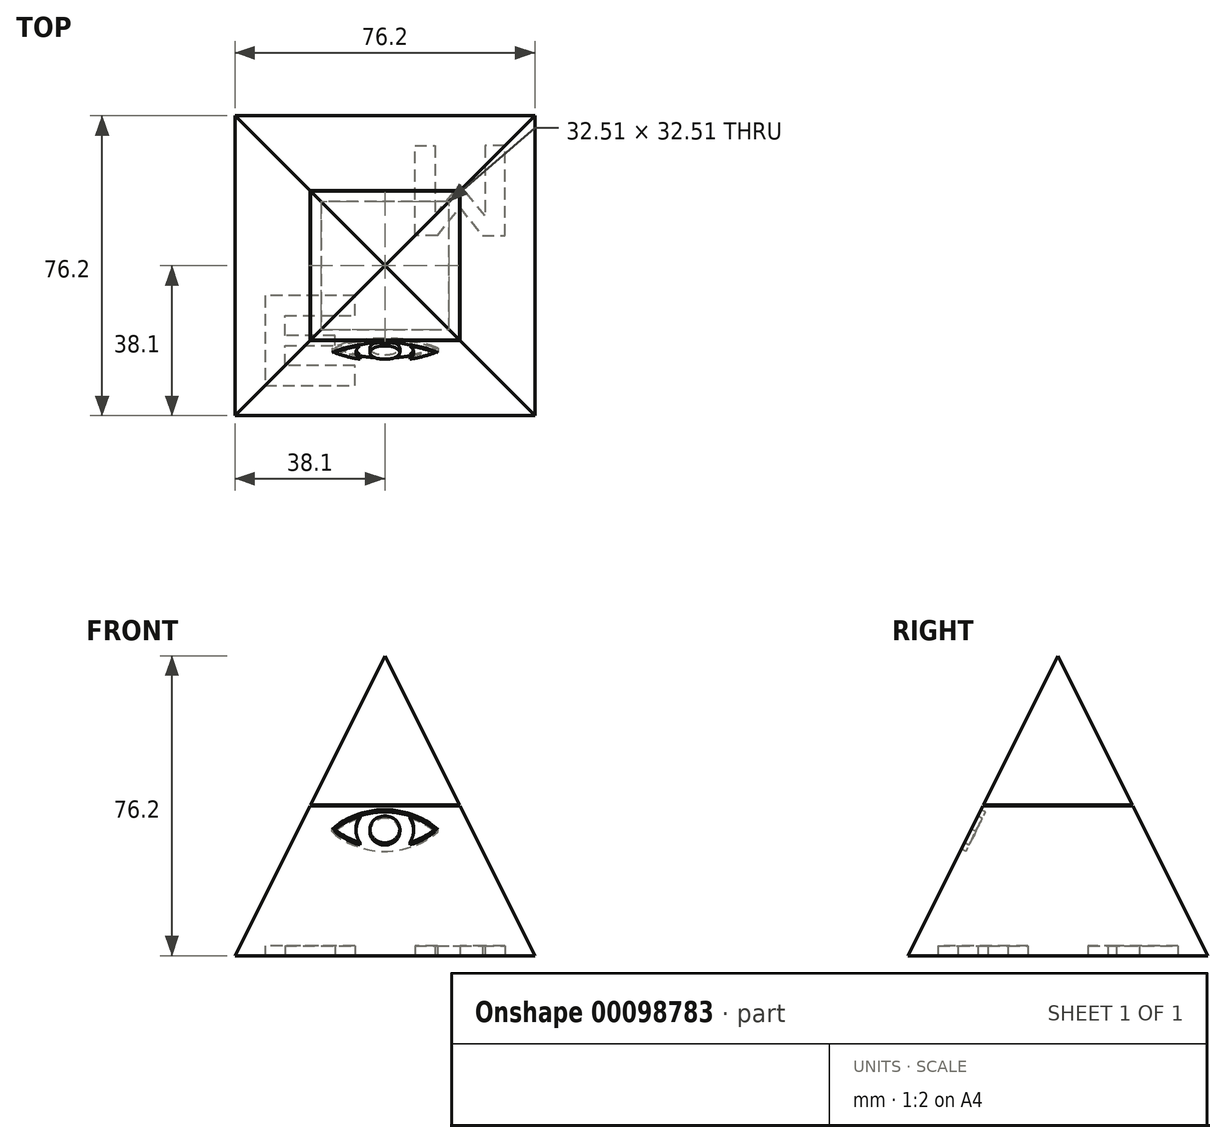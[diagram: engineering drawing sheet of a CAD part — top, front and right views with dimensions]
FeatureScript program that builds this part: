
annotation { "Feature Type Name" : "Feature", "Feature Type Description" : "" }
export const myFeature = defineFeature(function(context is Context, id is Id, definition is map)
    precondition{}
    {
        {
            var Q0;
            Q0=qCreatedBy(makeId("Front.planeOp"),FACE);
            var sketch = newSketch(context, id + "F0", { "sketchPlane" : qUnion([Q0])});
            skLineSegment(sketch, "E0", {"start": v(-38.1, 0) * mm, "end": v(-38.1, 38.1) * mm});
            skLineSegment(sketch, "E1", {"start": v(-38.1, 38.1) * mm, "end": v(0, 38.1) * mm});
            skLineSegment(sketch, "E2", {"start": v(0, 38.1) * mm, "end": v(38.1, 38.1) * mm});
            skLineSegment(sketch, "E3", {"start": v(38.1, 38.1) * mm, "end": v(38.1, 0) * mm});
            skLineSegment(sketch, "E4", {"start": v(38.1, 0) * mm, "end": v(38.1, -38.1) * mm});
            skLineSegment(sketch, "E5", {"start": v(38.1, -38.1) * mm, "end": v(0, -38.1) * mm});
            skLineSegment(sketch, "E6", {"start": v(0, -38.1) * mm, "end": v(-38.1, -38.1) * mm});
            skLineSegment(sketch, "E7", {"start": v(-38.1, -38.1) * mm, "end": v(-38.1, 0) * mm});
            skSolve(sketch);
        }
        {
            var Q0;
            Q0 = qSketchRegion(id + "F0", true);
            extrude(context, id + "F1", {"entities" : qUnion([Q0]), "depth" : 38.1 * mm});
        }
        {
            var Q0;
            Q0 = qSketchRegion(id + "F0", true);
            extrude(context, id + "F2", {"entities" : qUnion([Q0]), "operationType" : NewBodyOperationType.ADD, "oppositeDirection" : true, "depth" : 38.1 * mm});
        }
        {
            var Q0;
            Q0=makeQuery(id+"F1.opExtrude","CAP_FACE",FACE,{"disambiguationData":[OSD([sQuery(id+"F0.wireOp",EDGE,"E0"),sQuery(id+"F0.wireOp",EDGE,"E1"),sQuery(id+"F0.wireOp",EDGE,"E2"),sQuery(id+"F0.wireOp",EDGE,"E3"),sQuery(id+"F0.wireOp",EDGE,"E4"),sQuery(id+"F0.wireOp",EDGE,"E5"),sQuery(id+"F0.wireOp",EDGE,"E6"),sQuery(id+"F0.wireOp",EDGE,"E7")])],"isStart":false});
            var sketch = newSketch(context, id + "F3", { "sketchPlane" : qUnion([Q0])});
            skLineSegment(sketch, "E8", {"start": v(-38.1, -38.1) * mm, "end": v(0, 38.1) * mm});
            skLineSegment(sketch, "E9", {"start": v(0, 38.1) * mm, "end": v(38.1, -38.1) * mm});
            skLineSegment(sketch, "E10", {"start": v(38.1, -38.1) * mm, "end": v(-38.1, -38.1) * mm});
            skSolve(sketch);
        }
        {
            var Q0;
            {var subQ0=sQuery(id+"F0.wireOp",EDGE,"E7");var subQ1=sQuery(id+"F0.wireOp",EDGE,"E0");Q0=makeQuery(id+"F2.boolean.opBoolean","MERGE",FACE,{"derivedFrom":[makeQuery(id+"F1.opExtrude","SWEPT_FACE",FACE,{"disambiguationData":[OSD([subQ1,subQ0])]}),makeQuery(id+"F2.opExtrude","SWEPT_FACE",FACE,{"disambiguationData":[OSD([subQ1,subQ0])]})]});}
            var sketch = newSketch(context, id + "F4", { "sketchPlane" : qUnion([Q0])});
            skLineSegment(sketch, "E11", {"start": v(-38.1, -38.1) * mm, "end": v(0, 38.1) * mm});
            skLineSegment(sketch, "E12", {"start": v(0, 38.1) * mm, "end": v(38.1, -38.1) * mm});
            skLineSegment(sketch, "E13", {"start": v(38.1, -38.1) * mm, "end": v(-38.1, -38.1) * mm});
            skSolve(sketch);
        }
        {
            var Q0;
            {var subQ0=sQuery(id+"F4.wireOp",EDGE,"E11");Q0=makeQuery(id+"F4.imprint","IMPRINT",FACE,{"disambiguationData":[TD([[makeQuery(id+"F4.imprint","IMPRINT",EDGE,{"derivedFrom":subQ0}),1.0]])]});}
            var Q1;
            {var subQ0=sQuery(id+"F4.wireOp",EDGE,"E12");Q1=makeQuery(id+"F4.imprint","IMPRINT",FACE,{"disambiguationData":[TD([[makeQuery(id+"F4.imprint","IMPRINT",EDGE,{"derivedFrom":subQ0}),1.0]])]});}
            extrude(context, id + "F5", {"entities" : qUnion([Q0, Q1]), "operationType" : NewBodyOperationType.REMOVE, "oppositeDirection" : true, "depth" : 76.2 * mm});
        }
        {
            var Q0;
            {var subQ0=sQuery(id+"F3.wireOp",EDGE,"E8");Q0=makeQuery(id+"F3.imprint","IMPRINT",FACE,{"disambiguationData":[TD([[makeQuery(id+"F3.imprint","IMPRINT",EDGE,{"derivedFrom":subQ0}),1.0]])]});}
            var Q1;
            {var subQ0=sQuery(id+"F3.wireOp",EDGE,"E9");Q1=makeQuery(id+"F3.imprint","IMPRINT",FACE,{"disambiguationData":[TD([[makeQuery(id+"F3.imprint","IMPRINT",EDGE,{"derivedFrom":subQ0}),1.0]])]});}
            extrude(context, id + "F6", {"entities" : qUnion([Q0, Q1]), "operationType" : NewBodyOperationType.REMOVE, "oppositeDirection" : true, "depth" : 76.2 * mm});
        }
        {
            var Q0;
            Q0=makeQuery(id+"F5.boolean.opBoolean","COPY",FACE,{"derivedFrom":makeQuery(id+"F5.opExtrude","SWEPT_FACE",FACE,{"disambiguationData":[OSD([sQuery(id+"F4.wireOp",EDGE,"E12")])]})});
            var sketch = newSketch(context, id + "F7", { "sketchPlane" : qUnion([Q0])});
            skArc(sketch, "E14", {"start": v(12.7, -15.24) * mm, "mid": v(0, -10.39) * mm, "end": v(-12.7, -15.24) * mm});
            skArc(sketch, "E15", {"start": v(-12.7, -15.24) * mm, "mid": v(0, -20.1) * mm, "end": v(12.7, -15.24) * mm});
            skArc(sketch, "E16", {"start": v(-6.35, -11.48) * mm, "mid": v(-7.34, -15.24) * mm, "end": v(-6.35, -19) * mm});
            skArc(sketch, "E17", {"start": v(6.35, -19) * mm, "mid": v(7.34, -15.24) * mm, "end": v(6.35, -11.48) * mm});
            skCircle(sketch, "E18", {"center": v(0, -15.24) * mm, "radius": 3.81 * mm});
            skArc(sketch, "E19", {"start": v(13.46, -15.24) * mm, "mid": v(0, -9.67) * mm, "end": v(-13.46, -15.24) * mm});
            skArc(sketch, "E20", {"start": v(-13.46, -15.24) * mm, "mid": v(0, -20.81) * mm, "end": v(13.46, -15.24) * mm});
            skSolve(sketch);
        }
        {
            var Q0;
            Q0=makeQuery(id+"F7.imprint","IMPRINT",FACE,{"disambiguationData":[TD([[makeQuery(id+"F7.imprint","IMPRINT",EDGE,{"derivedFrom":sQuery(id+"F7.wireOp",EDGE,"E19")}),1.0]])]});
            var Q1;
            {var subQ1=sQuery(id+"F7.wireOp",EDGE,"E16");Q1=makeQuery(id+"F7.imprint","IMPRINT",FACE,{"disambiguationData":[TD([[makeQuery(id+"F7.imprint","IMPRINT",EDGE,{"derivedFrom":subQ1}),1.0]])]});}
            extrude(context, id + "F8", {"entities" : qUnion([Q0, Q1]), "operationType" : NewBodyOperationType.REMOVE, "oppositeDirection" : true, "depth" : 1.27 * mm});
        }
        {
            var Q0;
            {var subQ0=sQuery(id+"F0.wireOp",EDGE,"E6");var subQ1=sQuery(id+"F0.wireOp",EDGE,"E5");Q0=makeQuery(id+"F2.boolean.opBoolean","MERGE",FACE,{"derivedFrom":[makeQuery(id+"F1.opExtrude","SWEPT_FACE",FACE,{"disambiguationData":[OSD([subQ1,subQ0])]}),makeQuery(id+"F2.opExtrude","SWEPT_FACE",FACE,{"disambiguationData":[OSD([subQ1,subQ0])]})]});}
            var sketch = newSketch(context, id + "F9", { "sketchPlane" : qUnion([Q0])});
            skPoint(sketch, "E21.endSnap0", {"position": v(-38.1, 0) * mm});
            skPoint(sketch, "E22.endSnap0", {"position": v(0, 38.1) * mm});
            skLineSegment(sketch, "E23", {"start": v(-7.62, 7.62) * mm, "end": v(-30.48, 7.62) * mm});
            skLineSegment(sketch, "E24", {"start": v(-30.48, 7.62) * mm, "end": v(-30.48, 30.48) * mm});
            skLineSegment(sketch, "E25", {"start": v(-30.48, 30.48) * mm, "end": v(-7.62, 30.48) * mm});
            skLineSegment(sketch, "E26", {"start": v(-7.62, 30.48) * mm, "end": v(-7.62, 25.4) * mm});
            skLineSegment(sketch, "E27", {"start": v(-7.62, 25.4) * mm, "end": v(-25.4, 25.4) * mm});
            skLineSegment(sketch, "E28", {"start": v(-25.4, 25.4) * mm, "end": v(-25.4, 20.32) * mm});
            skLineSegment(sketch, "E29", {"start": v(-25.4, 20.32) * mm, "end": v(-12.7, 20.32) * mm});
            skLineSegment(sketch, "E30", {"start": v(-12.7, 20.32) * mm, "end": v(-12.7, 17.78) * mm});
            skLineSegment(sketch, "E31", {"start": v(-12.7, 17.78) * mm, "end": v(-25.4, 17.78) * mm});
            skLineSegment(sketch, "E32", {"start": v(-25.4, 17.78) * mm, "end": v(-25.4, 12.7) * mm});
            skLineSegment(sketch, "E33", {"start": v(-25.4, 12.7) * mm, "end": v(-7.62, 12.7) * mm});
            skLineSegment(sketch, "E34", {"start": v(-7.62, 12.7) * mm, "end": v(-7.62, 7.62) * mm});
            skLineSegment(sketch, "E35", {"start": v(0, 0) * mm, "end": v(7.62, 0) * mm});
            skLineSegment(sketch, "E36", {"start": v(7.62, 0) * mm, "end": v(7.62, -7.62) * mm});
            skLineSegment(sketch, "E37", {"start": v(38.1, 0) * mm, "end": v(38.1, -7.62) * mm});
            skLineSegment(sketch, "E38", {"start": v(0, -38.1) * mm, "end": v(7.62, -38.1) * mm});
            skLineSegment(sketch, "E39", {"start": v(38.1, -38.1) * mm, "end": v(30.48, -38.1) * mm});
            skLineSegment(sketch, "E40", {"start": v(30.48, -7.62) * mm, "end": v(30.48, -30.48) * mm});
            skLineSegment(sketch, "E41", {"start": v(30.48, -30.48) * mm, "end": v(25.4, -30.48) * mm});
            skLineSegment(sketch, "E42", {"start": v(25.4, -30.48) * mm, "end": v(25.4, -12.7) * mm});
            skLineSegment(sketch, "E43", {"start": v(25.4, -12.7) * mm, "end": v(19.05, -20.63) * mm});
            skLineSegment(sketch, "E44", {"start": v(12.7, -12.7) * mm, "end": v(19.05, -20.63) * mm});
            skLineSegment(sketch, "E45", {"start": v(7.62, -30.48) * mm, "end": v(12.7, -30.48) * mm});
            skLineSegment(sketch, "E46", {"start": v(12.7, -30.48) * mm, "end": v(12.7, -12.7) * mm});
            skLineSegment(sketch, "E47", {"start": v(7.62, -7.62) * mm, "end": v(7.62, -30.48) * mm});
            skLineSegment(sketch, "E48", {"start": v(13.33, -7.62) * mm, "end": v(19.05, -14.76) * mm});
            skLineSegment(sketch, "E49", {"start": v(19.05, -14.76) * mm, "end": v(24.77, -7.62) * mm});
            skLineSegment(sketch, "E50", {"start": v(13.33, -7.62) * mm, "end": v(7.62, -7.62) * mm});
            skLineSegment(sketch, "E51", {"start": v(24.77, -7.62) * mm, "end": v(30.48, -7.62) * mm});
            skSolve(sketch);
        }
        {
            var Q0;
            Q0=makeQuery(id+"F9.imprint","IMPRINT",FACE,{"disambiguationData":[TD([[makeQuery(id+"F9.imprint","IMPRINT",EDGE,{"derivedFrom":sQuery(id+"F9.wireOp",EDGE,"E23")}),-1.0]])]});
            var Q1;
            Q1=makeQuery(id+"F9.imprint","IMPRINT",FACE,{"disambiguationData":[TD([[makeQuery(id+"F9.imprint","IMPRINT",EDGE,{"derivedFrom":sQuery(id+"F9.wireOp",EDGE,"E40")}),-1.0]])]});
            extrude(context, id + "F10", {"entities" : qUnion([Q0, Q1]), "operationType" : NewBodyOperationType.REMOVE, "oppositeDirection" : true, "depth" : 2.54 * mm});
        }
        {
            var Q0;
            Q0=qCreatedBy(makeId("Top.planeOp"),FACE);
            var sketch = newSketch(context, id + "F11", { "sketchPlane" : qUnion([Q0])});
            skLineSegment(sketch, "E52", {"start": v(-38.1, 0) * mm, "end": v(-38.1, 38.1) * mm});
            skLineSegment(sketch, "E53", {"start": v(-38.1, 38.1) * mm, "end": v(38.1, 38.1) * mm});
            skLineSegment(sketch, "E54", {"start": v(38.1, 38.1) * mm, "end": v(38.1, -38.1) * mm});
            skLineSegment(sketch, "E55", {"start": v(38.1, -38.1) * mm, "end": v(-38.1, -38.1) * mm});
            skLineSegment(sketch, "E56", {"start": v(-38.1, -38.1) * mm, "end": v(-38.1, 0) * mm});
            skSolve(sketch);
        }
        {
            var Q0;
            Q0 = qSketchRegion(id + "F11", true);
            extrude(context, id + "F12", {"entities" : qUnion([Q0]), "operationType" : NewBodyOperationType.REMOVE, "depth" : 0.25 * mm});
        }
        {
            var Q0;
            Q0=makeQuery(id+"F12.boolean.opBoolean","SPLIT",BODY,{"disambiguationData":[OD(1.0)],"derivedFrom":makeQuery(id+"F1.opExtrude","SWEPT_BODY",BODY,{"disambiguationData":[OSD([sQuery(id+"F0.wireOp",EDGE,"E0"),sQuery(id+"F0.wireOp",EDGE,"E1"),sQuery(id+"F0.wireOp",EDGE,"E2"),sQuery(id+"F0.wireOp",EDGE,"E3"),sQuery(id+"F0.wireOp",EDGE,"E4"),sQuery(id+"F0.wireOp",EDGE,"E5"),sQuery(id+"F0.wireOp",EDGE,"E6"),sQuery(id+"F0.wireOp",EDGE,"E7")])]})});
            var Q1;
            {var subQ0=sQuery(id+"F0.wireOp",EDGE,"E7");var subQ1=sQuery(id+"F0.wireOp",EDGE,"E6");Q1=makeQuery(id+"F6.boolean.opBoolean","MERGE",EDGE,{"derivedFrom":[makeQuery(id+"F2.boolean.opBoolean","MERGE",EDGE,{"derivedFrom":[makeQuery(id+"F1.opExtrude","SWEPT_EDGE",EDGE,{"disambiguationData":[OSD([subQ1,subQ0])]}),makeQuery(id+"F2.opExtrude","SWEPT_EDGE",EDGE,{"disambiguationData":[OSD([subQ1,subQ0])]})]}),makeQuery(id+"F6.opExtrude","SWEPT_EDGE",EDGE,{"disambiguationData":[OSD([sQuery(id+"F0.wireOp",EDGE,"E0"),subQ0,sQuery(id+"F3.wireOp",EDGE,"E8"),sQuery(id+"F3.wireOp",EDGE,"E10")])]})]});}
            transform(context, id + "F13", {"entities" : qUnion([Q0]), "transformType" : TransformType.TRANSLATION_ENTITY, "oppositeDirectionEntity" : false, "transformLine" : qUnion([Q1]), "makeCopy" : false});
        }
        {
            var Q0;
            Q0=makeQuery(id+"F12.boolean.opBoolean","COPY",FACE,{"derivedFrom":makeQuery(id+"F12.opExtrude","CAP_FACE",FACE,{"disambiguationData":[OSD([sQuery(id+"F11.wireOp",EDGE,"E52"),sQuery(id+"F11.wireOp",EDGE,"E53"),sQuery(id+"F11.wireOp",EDGE,"E54"),sQuery(id+"F11.wireOp",EDGE,"E55"),sQuery(id+"F11.wireOp",EDGE,"E56")])],"isStart":true})});
            var sketch = newSketch(context, id + "F14", { "sketchPlane" : qUnion([Q0])});
            skLineSegment(sketch, "E57", {"start": v(-16.51, 16.5) * mm, "end": v(16.5, 16.5) * mm});
            skLineSegment(sketch, "E58", {"start": v(16.5, 16.5) * mm, "end": v(16.5, -16.51) * mm});
            skLineSegment(sketch, "E59", {"start": v(16.5, -16.51) * mm, "end": v(-16.51, -16.51) * mm});
            skLineSegment(sketch, "E60", {"start": v(-16.51, -16.51) * mm, "end": v(-16.51, 16.5) * mm});
            skSolve(sketch);
        }
        {
            var Q0;
            Q0=makeQuery(id+"F14.imprint","IMPRINT",FACE,{"disambiguationData":[TD([[makeQuery(id+"F14.imprint","IMPRINT",EDGE,{"derivedFrom":sQuery(id+"F14.wireOp",EDGE,"E57")}),-1.0]])]});
            extrude(context, id + "F15", {"entities" : qUnion([Q0]), "operationType" : NewBodyOperationType.REMOVE, "oppositeDirection" : true, "depth" : 33.02 * mm});
        }
        {
            var Q0;
            Q0=makeQuery(id+"F12.boolean.opBoolean","COPY",FACE,{"derivedFrom":makeQuery(id+"F12.opExtrude","CAP_FACE",FACE,{"disambiguationData":[OSD([sQuery(id+"F11.wireOp",EDGE,"E52"),sQuery(id+"F11.wireOp",EDGE,"E53"),sQuery(id+"F11.wireOp",EDGE,"E54"),sQuery(id+"F11.wireOp",EDGE,"E55"),sQuery(id+"F11.wireOp",EDGE,"E56")])],"isStart":false})});
            var sketch = newSketch(context, id + "F16", { "sketchPlane" : qUnion([Q0])});
            skLineSegment(sketch, "E61", {"start": v(-18.92, -95.12) * mm, "end": v(18.92, -95.12) * mm});
            skLineSegment(sketch, "E62", {"start": v(-16.26, -92.46) * mm, "end": v(-16.26, -59.94) * mm});
            skLineSegment(sketch, "E63", {"start": v(-16.26, -59.94) * mm, "end": v(16.26, -59.94) * mm});
            skLineSegment(sketch, "E64", {"start": v(16.26, -59.94) * mm, "end": v(16.26, -92.46) * mm});
            skLineSegment(sketch, "E65", {"start": v(16.26, -92.46) * mm, "end": v(-16.26, -92.46) * mm});
            skSolve(sketch);
        }
        {
            var Q0;
            Q0=makeQuery(id+"F16.imprint","IMPRINT",FACE,{"disambiguationData":[TD([[makeQuery(id+"F16.imprint","IMPRINT",EDGE,{"derivedFrom":sQuery(id+"F16.wireOp",EDGE,"E62")}),-1.0]])]});
            extrude(context, id + "F17", {"entities" : qUnion([Q0]), "operationType" : NewBodyOperationType.ADD, "depth" : 2.54 * mm});
        }
        {
            var Q0;
            Q0=qCreatedBy(makeId("Front.planeOp"),FACE);
            var sketch = newSketch(context, id + "F18", { "sketchPlane" : qUnion([Q0])});
            skLineSegment(sketch, "E66", {"start": v(0, -33.08) * mm, "end": v(-33.02, -33.08) * mm});
            skLineSegment(sketch, "E67", {"start": v(0, 0) * mm, "end": v(-16.51, 0) * mm});
            skLineSegment(sketch, "E68", {"start": v(-16.5, 0) * mm, "end": v(-33.02, -33.08) * mm});
            skLineSegment(sketch, "E69", {"start": v(0, 0) * mm, "end": v(16.51, 0) * mm});
            skLineSegment(sketch, "E70", {"start": v(0, -33.08) * mm, "end": v(33.02, -33.08) * mm});
            skLineSegment(sketch, "E71", {"start": v(33.02, -33.08) * mm, "end": v(16.51, 0) * mm});
            skSolve(sketch);
        }
        {
            var Q0;
            Q0 = qSketchRegion(id + "F18", true);
            extrude(context, id + "F19", {"entities" : qUnion([Q0]), "operationType" : NewBodyOperationType.REMOVE, "oppositeDirection" : true, "depth" : 16.5 * mm});
        }
        {
            var Q0;
            Q0 = qSketchRegion(id + "F18", true);
            extrude(context, id + "F20", {"entities" : qUnion([Q0]), "operationType" : NewBodyOperationType.REMOVE, "depth" : 16.5 * mm});
        }
        {
            var Q0;
            Q0=qCreatedBy(makeId("Right.planeOp"),FACE);
            var sketch = newSketch(context, id + "F21", { "sketchPlane" : qUnion([Q0])});
            skLineSegment(sketch, "E72", {"start": v(0, -33.02) * mm, "end": v(-33.02, -33.02) * mm});
            skLineSegment(sketch, "E73", {"start": v(0, -33.02) * mm, "end": v(33.02, -33.02) * mm});
            skLineSegment(sketch, "E74", {"start": v(0, 0) * mm, "end": v(-16.51, 0) * mm});
            skLineSegment(sketch, "E75", {"start": v(0, 0) * mm, "end": v(16.51, 0) * mm});
            skLineSegment(sketch, "E76", {"start": v(-33.02, -33.02) * mm, "end": v(-16.5, 0) * mm});
            skLineSegment(sketch, "E77", {"start": v(16.51, 0) * mm, "end": v(33.02, -33.02) * mm});
            skSolve(sketch);
        }
        {
            var Q0;
            Q0 = qSketchRegion(id + "F21", true);
            extrude(context, id + "F22", {"entities" : qUnion([Q0]), "operationType" : NewBodyOperationType.REMOVE, "oppositeDirection" : true, "depth" : 16.5 * mm});
        }
        {
            var Q0;
            Q0 = qSketchRegion(id + "F21", true);
            extrude(context, id + "F23", {"entities" : qUnion([Q0]), "operationType" : NewBodyOperationType.REMOVE, "depth" : 16.5 * mm});
        }
    });
